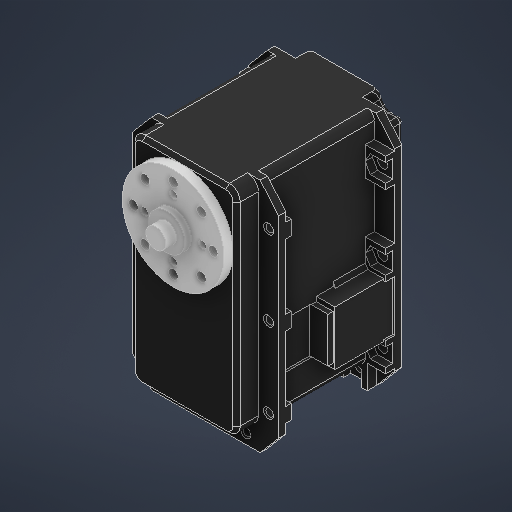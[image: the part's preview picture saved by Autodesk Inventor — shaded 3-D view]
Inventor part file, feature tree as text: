
AUTODESK INVENTOR PART (.ipt)
format: ipt  version: 2025 (Build 290162000, 162)  size: 556,032 bytes
history: native  units: in
note: dims shown in document units (in); Inventor stores cm internally (conversion verified against a paired STEP export)
features: thread x8, sketch x3, extrude x1, imported_body x1
ambient origin geometry x8: Origin, YZ Plane, XZ Plane, XY Plane, X Axis, Y Axis, Z Axis, Center Point
bodies: Solid1 (feature_tree)
feature tree (13):
  extrude  "Extrusion1"  Depth=0.315in
  thread  "Thread1"  [1 undecoded]
  thread  "Thread2"  [1 undecoded]
  thread  "Thread3"  [1 undecoded]
  thread  "Thread4"  [1 undecoded]
  thread  "Thread5"  [1 undecoded]
  thread  "Thread6"  [1 undecoded]
  thread  "Thread7"  [1 undecoded]
  thread  "Thread8"  [1 undecoded]
  sketch  "Sketch1"  dims[d0=0.0787in d1=0.315in d2=1.5748in d4=360.0deg d6=0.0984in d7=0.4331in d8=3.1496in d10=360.0deg d12=0.0in d13=0.0in d14=0.0984in d15=0.0in d16=0.0984in d17=0.0in d18=0.0984in d19=0.0in]
  sketch  "Sketch Circular Pattern1"  dims[d20=0.0984in d21=0.0in]
  sketch  "Sketch Circular Pattern2"  dims[d22=0.0984in d23=0.0in d24=0.0984in d25=0.0in d26=0.0984in d27=0.0in d28=0.0984in d29=0.0in]
  imported_body  "Base1"
note: 8 required parameter values undecoded (feature->parameter linkage not recoverable at this tier; creation-order binding heuristic only, values carry confidence <= 0.55)
